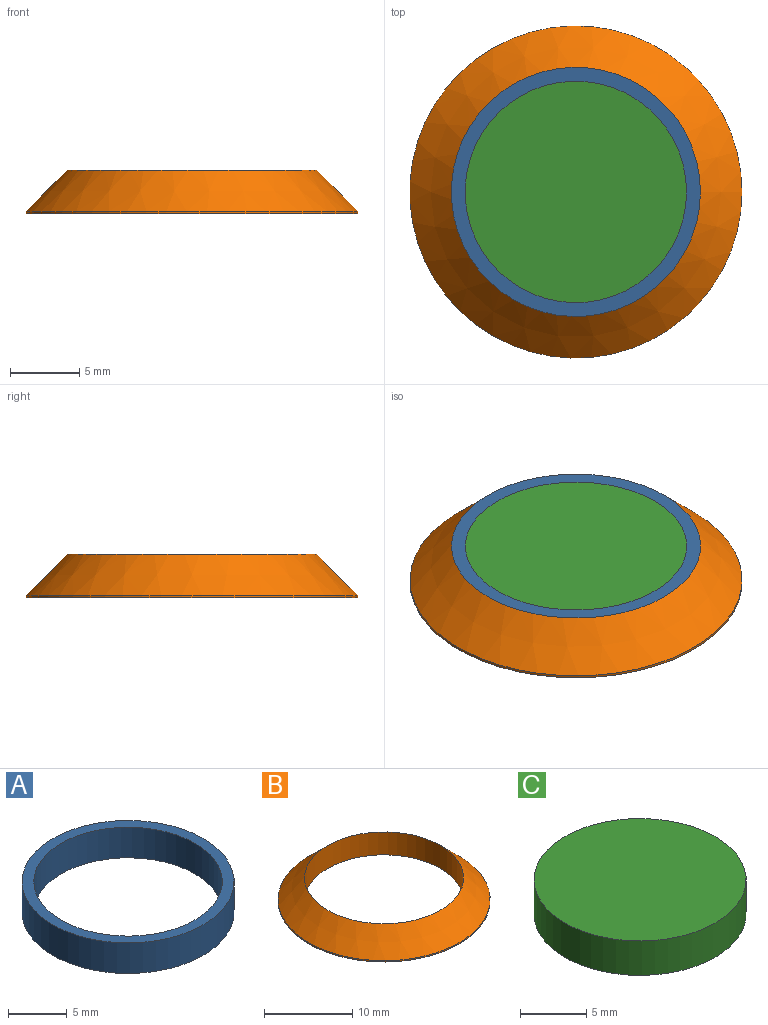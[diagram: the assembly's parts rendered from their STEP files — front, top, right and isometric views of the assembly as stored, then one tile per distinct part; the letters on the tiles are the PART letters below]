
ASSEMBLY  parts=3 mates=2
PART A: 4 faces, bbox 18x18x3.2 mm
  f0: cylinder r=8mm len=16mm, axis (0,0,-1), area 159.6mm2, adj f2,f3
  f1: cylinder r=9mm len=18mm, axis (0,0,-1), area 179.5mm2, adj f2,f3
  f2: plane 18x18mm, normal (0,0,1), area 53.4mm2, adj f0,f1
  f3: plane 18x18mm, normal (0,0,-1), area 53.4mm2, adj f0,f1
PART B: 4 faces, bbox 24x24x3.2 mm
  f0: cylinder r=9mm len=18mm, axis (0,0,-1), area 179.5mm2, adj f2,f3
  f1: cylinder r=12mm len=24mm, axis (0,0,-1), area 13.2mm2, adj f2,f3
  f2: plane 24x24mm, normal (0,0,-1), area 197.9mm2, adj f0,f1
  f3: cone r=9mm half-angle=45deg, axis (0,0,-1), area 279.9mm2, adj f0,f1
PART C: 3 faces, bbox 16x16x3.2 mm
  f0: cylinder r=8mm len=16mm, axis (0,0,-1), area 159.6mm2, adj f1,f2
  f1: plane 16x16mm, normal (0,0,1), area 201.1mm2, adj f0
  f2: plane 16x16mm, normal (0,0,-1), area 201.1mm2, adj f0
PLACE A at identity
PLACE B at identity
PLACE C at identity
MATE fastened C.f0 <-> B.f1  axis (0,0,-1) through (0,0,0)mm
MATE fastened C.f0 <-> A.f1  axis (0,0,-1) through (0,0,0)mm
